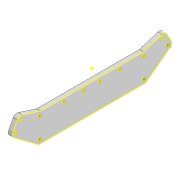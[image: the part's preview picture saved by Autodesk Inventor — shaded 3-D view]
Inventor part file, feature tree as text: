
AUTODESK INVENTOR PART (.ipt)
format: ipt  version: 2022 (Build 260153000, 153)  size: 284,672 bytes
history: native  units: mm
features: sketch x2, extrude x1, projected_geometry x1
ambient origin geometry x8: Origin, YZ Plane, XZ Plane, XY Plane, X Axis, Y Axis, Z Axis, Center Point
bodies: Solid1 (feature_tree)
feature tree (4):
  extrude  "Extrusion1"  Depth=3.9mm
  sketch  "Sketch8"  dims[d6=5.0mm d7=0.0mm d25=3.0mm d28=3.0mm d43=59.0mm d44=65.0mm d45=65.0mm d47=59.0mm d48=10.0mm d49=10.0mm d50=10.0mm d53=3.0mm d54=3.0mm d55=4.0mm d56=4.0mm d57=25.0mm d58=25.0mm d59=10.0mm d60=10.0mm d61=10.0mm d62=3.0mm d63=3.0mm d64=3.0mm d65=3.0mm d66=3.0mm d67=10.0mm d68=25.0mm d69=3.0mm d70=3.0mm d71=10.0mm d72=25.0mm d73=25.0mm d74=25.0mm d76=3.0mm d78=3.0mm d79=3.0mm d80=3.0mm d81=6.0mm d82=6.0mm d83=19.0mm d84=8.0mm d85=8.0mm d86=8.0mm d87=8.0mm d88=2.0mm d89=10.0mm d90=10.0mm d91=30.0mm d92=30.0mm]
  sketch  "Sketch1"  dims[d2=3.9mm d4=3.9mm]
  projected_geometry  "Project Cut Edges1"
